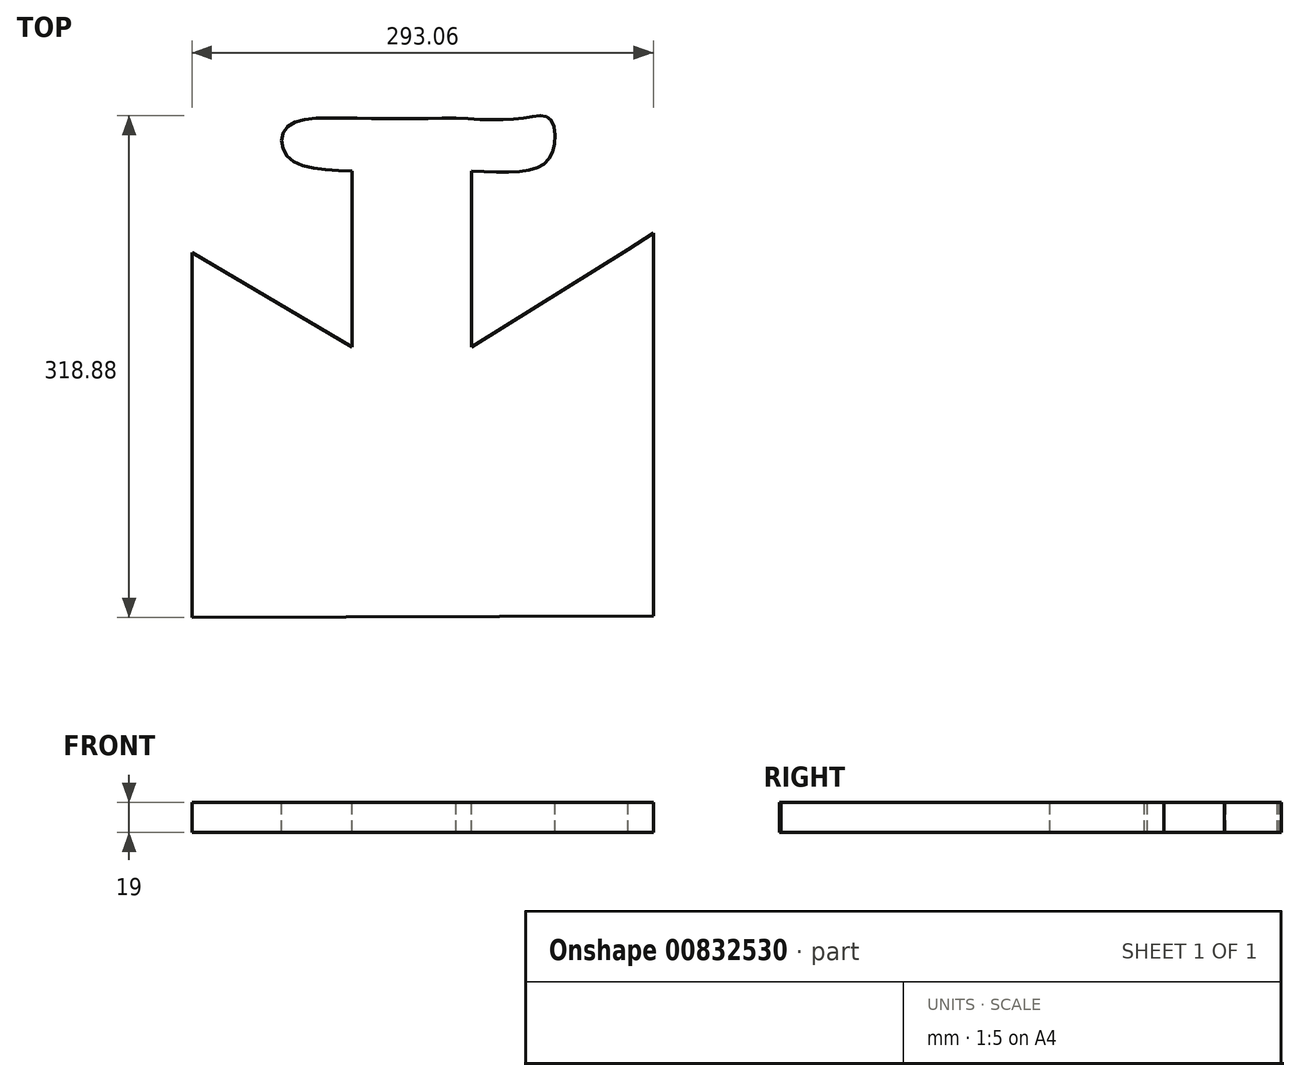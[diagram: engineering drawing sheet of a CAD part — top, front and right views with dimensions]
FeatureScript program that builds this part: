
annotation { "Feature Type Name" : "Feature", "Feature Type Description" : "" }
export const myFeature = defineFeature(function(context is Context, id is Id, definition is map)
    precondition{}
    {
        {
            var Q0;
            Q0=qCreatedBy(makeId("Top.planeOp"),FACE);
            var sketch = newSketch(context, id + "F0", { "sketchPlane" : qUnion([Q0])});
            skLineSegment(sketch, "E0.bottom", {"start": v(-200, -175) * mm, "end": v(200, -175) * mm});
            skLineSegment(sketch, "E0.top", {"start": v(-200, 175) * mm, "end": v(200, 175) * mm});
            skLineSegment(sketch, "E0.left", {"start": v(-200, -175) * mm, "end": v(-200, 175) * mm});
            skLineSegment(sketch, "E0.right", {"start": v(200, -175) * mm, "end": v(200, 175) * mm});
            skPoint(sketch, "E0.middle", {"position": v(0, 0) * mm});
            skSolve(sketch);
        }
        {
            var Q0;
            Q0=makeQuery(id+"F0.imprint","IMPRINT",FACE,{"disambiguationData":[TD([[makeQuery(id+"F0.imprint","IMPRINT",EDGE,{"derivedFrom":sQuery(id+"F0.wireOp",EDGE,"E0.bottom")}),1.0]])]});
            extrude(context, id + "F1", {"entities" : qUnion([Q0]), "depth" : 19 * mm, "offsetDistance" : 25 * mm});
        }
        {
            var Q0;
            Q0=makeQuery(id+"F1.opExtrude","CAP_FACE",FACE,{"disambiguationData":[OSD([sQuery(id+"F0.wireOp",EDGE,"E0.bottom"),sQuery(id+"F0.wireOp",EDGE,"E0.top"),sQuery(id+"F0.wireOp",EDGE,"E0.left"),sQuery(id+"F0.wireOp",EDGE,"E0.right")])],"isStart":false});
            var sketch = newSketch(context, id + "F2", { "sketchPlane" : qUnion([Q0])});
            skLineSegment(sketch, "E1", {"start": v(-177.46, -154.13) * mm, "end": v(-177.46, 77.59) * mm});
            skLineSegment(sketch, "E2", {"start": v(-177.46, 77.59) * mm, "end": v(-75.75, 17.82) * mm});
            skLineSegment(sketch, "E3", {"start": v(-75.75, 17.82) * mm, "end": v(-75.75, 129.5) * mm});
            skFitSpline(sketch, "E4", {"points": [v(-75.75, 129.5) * mm, v(-116.65, 138.4) * mm, v(-117.7, 156.75) * mm, v(-75.75, 163.04) * mm, v(-9.7, 163.04) * mm], "startDerivative": vector(-198.28, 6.58) * mm, "endDerivative": vector(206.17, 1.94) * mm});
            skFitSpline(sketch, "E5", {"points": [v(-9.7, 163.04) * mm, v(31.72, 163.04) * mm, v(49.54, 163.04) * mm, v(52.16, 143.64) * mm, v(40.63, 131.06) * mm, v(0, 129.5) * mm], "startDerivative": vector(176.52, -9.83) * mm, "endDerivative": vector(-186.98, 11.24) * mm});
            skLineSegment(sketch, "E6", {"start": v(0, 129.5) * mm, "end": v(0, 17.82) * mm});
            skLineSegment(sketch, "E7", {"start": v(0, 17.82) * mm, "end": v(99.35, 79.69) * mm});
            skLineSegment(sketch, "E8", {"start": v(99.35, 79.69) * mm, "end": v(115.6, 90.17) * mm});
            skLineSegment(sketch, "E9", {"start": v(115.6, 90.17) * mm, "end": v(115.6, -153.08) * mm});
            skLineSegment(sketch, "E10", {"start": v(115.6, -153.08) * mm, "end": v(-177.46, -154.13) * mm});
            skFitSpline(sketch, "E11", {"points": [v(-63.17, 139.98) * mm, v(-78.38, 142.07) * mm, v(-81.52, 153.08) * mm, v(0, 157.28) * mm], "startDerivative": vector(-70.62, -5.28) * mm, "endDerivative": vector(204.27, -13.4) * mm});
            skFitSpline(sketch, "E12", {"points": [v(0, 157.28) * mm, v(7.6, 157.28) * mm, v(10.22, 141.55) * mm, v(-63.17, 139.98) * mm], "startDerivative": vector(44.32, 14.89) * mm, "endDerivative": vector(-178.37, 24.16) * mm});
            skSolve(sketch);
        }
        {
            var Q0;
            Q0=makeQuery(id+"F2.imprint","IMPRINT",FACE,{"disambiguationData":[TD([[makeQuery(id+"F2.imprint","IMPRINT",EDGE,{"derivedFrom":sQuery(id+"F2.wireOp",EDGE,"E1")}),1.0]])]});
            extrude(context, id + "F3", {"entities" : qUnion([Q0]), "operationType" : NewBodyOperationType.REMOVE, "endBound" : BoundingType.THROUGH_ALL, "oppositeDirection" : true, "depth" : 25 * mm, "offsetDistance" : 25 * mm});
        }
    });
